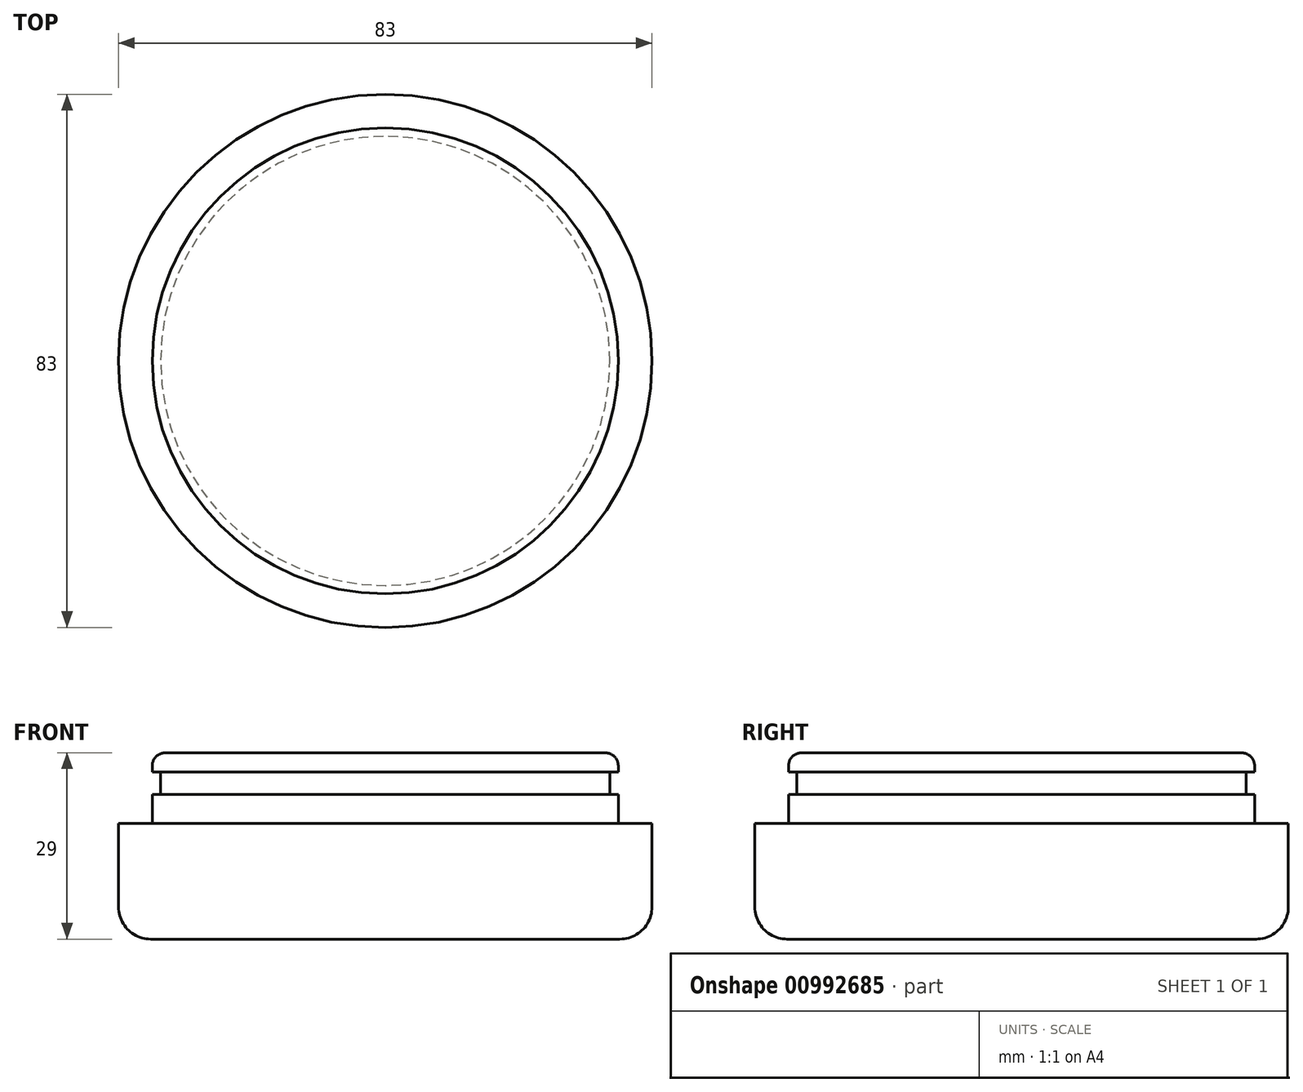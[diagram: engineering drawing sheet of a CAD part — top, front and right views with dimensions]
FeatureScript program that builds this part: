
annotation { "Feature Type Name" : "Feature", "Feature Type Description" : "" }
export const myFeature = defineFeature(function(context is Context, id is Id, definition is map)
    precondition{}
    {
        {
            var Q0;
            Q0=qCreatedBy(makeId("Front.planeOp"),FACE);
            var sketch = newSketch(context, id + "F0", { "sketchPlane" : qUnion([Q0])});
            skLineSegment(sketch, "E0.bottom", {"start": v(-36.25, 18) * mm, "end": v(-41.5, 18) * mm});
            skLineSegment(sketch, "E0.top", {"start": v(0, 0) * mm, "end": v(-41.5, 0) * mm});
            skLineSegment(sketch, "E0.left", {"start": v(0, 18) * mm, "end": v(0, 0) * mm});
            skLineSegment(sketch, "E0.right", {"start": v(-41.5, 18) * mm, "end": v(-41.5, 0) * mm});
            skLineSegment(sketch, "E1.top", {"start": v(-36.25, 29) * mm, "end": v(0, 29) * mm});
            skLineSegment(sketch, "E1.left", {"start": v(-36.25, 18) * mm, "end": v(-36.25, 22.5) * mm});
            skLineSegment(sketch, "E1.right", {"start": v(0, 18) * mm, "end": v(0, 29) * mm});
            skLineSegment(sketch, "E2.bottom", {"start": v(-36.25, 22.5) * mm, "end": v(-34.95, 22.5) * mm});
            skLineSegment(sketch, "E2.top", {"start": v(-36.25, 26) * mm, "end": v(-34.95, 26) * mm});
            skLineSegment(sketch, "E2.right", {"start": v(-34.95, 22.5) * mm, "end": v(-34.95, 26) * mm});
            skLineSegment(sketch, "E3.trimOffspring", {"start": v(-36.25, 26) * mm, "end": v(-36.25, 29) * mm});
            skSolve(sketch);
        }
        {
            var Q0;
            Q0=makeQuery(id+"F0.imprint","IMPRINT",FACE,{"disambiguationData":[TD([[makeQuery(id+"F0.imprint","IMPRINT",EDGE,{"derivedFrom":sQuery(id+"F0.wireOp",EDGE,"E0.bottom")}),1.0]])]});
            var Q1;
            Q1=sQuery(id+"F0.wireOp",EDGE,"E0.left");
            revolve(context, id + "F1", {"surfaceOperationType" : NewSurfaceOperationType.NEW, "entities" : qUnion([Q0]), "axis" : qUnion([Q1]), "revolveType" : RevolveType.FULL});
        }
        {
            var Q0;
            Q0=makeQuery(id+"F1.opRevolve","SWEPT_EDGE",EDGE,{"disambiguationData":[OSD([sQuery(id+"F0.wireOp",EDGE,"E0.top"),sQuery(id+"F0.wireOp",EDGE,"E0.right")])]});
            fillet(context, id + "F2", {"entities" : qUnion([Q0]), "radius" : 5 * mm, "tangentPropagation" : true, "allowEdgeOverflow" : false});
        }
        {
            var Q0;
            Q0=makeQuery(id+"F1.opRevolve","SWEPT_EDGE",EDGE,{"disambiguationData":[OSD([sQuery(id+"F0.wireOp",EDGE,"E1.top"),sQuery(id+"F0.wireOp",EDGE,"E3.trimOffspring")])]});
            fillet(context, id + "F3", {"entities" : qUnion([Q0]), "radius" : 2 * mm, "tangentPropagation" : true, "allowEdgeOverflow" : false});
        }
    });
